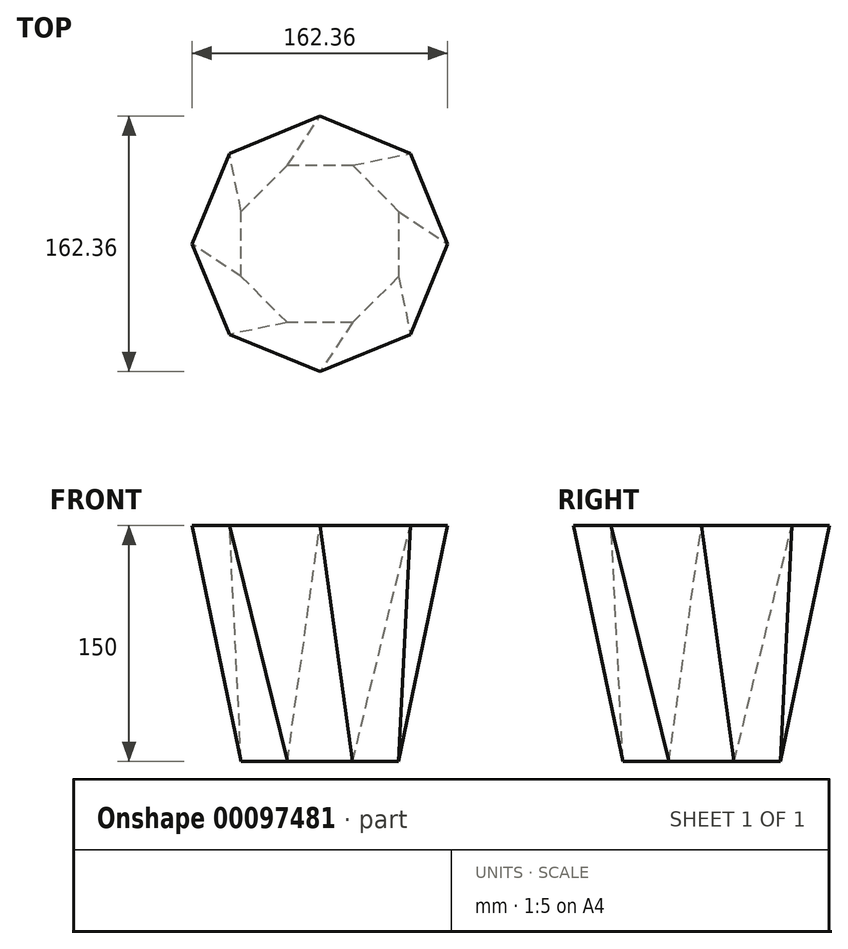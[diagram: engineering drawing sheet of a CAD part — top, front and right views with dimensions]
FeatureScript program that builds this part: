
annotation { "Feature Type Name" : "Feature", "Feature Type Description" : "" }
export const myFeature = defineFeature(function(context is Context, id is Id, definition is map)
    precondition{}
    {
        {
            assignVariable(context, id + "F0", {"name" : "height", "anyValue" : 150});
        }
        {
            var Q0;
            Q0=qCreatedBy(makeId("Top.planeOp"),FACE);
            var sketch = newSketch(context, id + "F1", { "sketchPlane" : qUnion([Q0])});
            skCircle(sketch, "E0.cCircle", {"center": v(0, 0) * mm, "radius": 50 * mm, "construction": true});
            skLineSegment(sketch, "E0.0", {"start": v(-50, 20.71) * mm, "end": v(-20.71, 50) * mm});
            skLineSegment(sketch, "E0.1", {"start": v(-20.71, 50) * mm, "end": v(20.71, 50) * mm});
            skLineSegment(sketch, "E0.2", {"start": v(20.71, 50) * mm, "end": v(50, 20.71) * mm});
            skLineSegment(sketch, "E0.3", {"start": v(50, 20.71) * mm, "end": v(50, -20.71) * mm});
            skLineSegment(sketch, "E0.4", {"start": v(50, -20.71) * mm, "end": v(20.71, -50) * mm});
            skLineSegment(sketch, "E0.5", {"start": v(20.71, -50) * mm, "end": v(-20.71, -50) * mm});
            skLineSegment(sketch, "E0.6", {"start": v(-20.71, -50) * mm, "end": v(-50, -20.71) * mm});
            skLineSegment(sketch, "E0.7", {"start": v(-50, -20.71) * mm, "end": v(-50, 20.71) * mm});
            skPoint(sketch, "E0.0.midPoint", {"position": v(-35.36, 35.36) * mm});
            skSolve(sketch);
        }
        {
            var Q0;
            Q0=qCreatedBy(makeId("Top.planeOp"),FACE);
            cPlane(context, id + "F2", {"entities" : qUnion([Q0]), "cplaneType" : CPlaneType.OFFSET, "offset" : (getVariable(context, 'height')) * mm, "width" : 150 * mm, "height" : 150 * mm});
        }
        {
            var Q0;
            Q0=qCreatedBy(id+"F2.planeOp",FACE);
            var sketch = newSketch(context, id + "F3", { "sketchPlane" : qUnion([Q0])});
            skCircle(sketch, "E1.cCircle", {"center": v(0, 0) * mm, "radius": 75 * mm, "construction": true});
            skLineSegment(sketch, "E1.0", {"start": v(-81.18, 0) * mm, "end": v(-57.4, 57.4) * mm});
            skLineSegment(sketch, "E1.1", {"start": v(-57.4, 57.4) * mm, "end": v(0, 81.18) * mm});
            skLineSegment(sketch, "E1.2", {"start": v(0, 81.18) * mm, "end": v(57.4, 57.4) * mm});
            skLineSegment(sketch, "E1.3", {"start": v(57.4, 57.4) * mm, "end": v(81.18, 0) * mm});
            skLineSegment(sketch, "E1.4", {"start": v(81.18, 0) * mm, "end": v(57.4, -57.4) * mm});
            skLineSegment(sketch, "E1.5", {"start": v(57.4, -57.4) * mm, "end": v(0, -81.18) * mm});
            skLineSegment(sketch, "E1.6", {"start": v(0, -81.18) * mm, "end": v(-57.4, -57.4) * mm});
            skLineSegment(sketch, "E1.7", {"start": v(-57.4, -57.4) * mm, "end": v(-81.18, 0) * mm});
            skPoint(sketch, "E1.0.midPoint", {"position": v(-69.3, 28.7) * mm});
            skSolve(sketch);
        }
        {
            var Q0;
            Q0=makeQuery(id+"F1.imprint","IMPRINT",FACE,{"disambiguationData":[TD([[makeQuery(id+"F1.imprint","IMPRINT",EDGE,{"derivedFrom":sQuery(id+"F1.wireOp",EDGE,"E0.0")}),-1.0]])]});
            var Q1;
            Q1=makeQuery(id+"F3.imprint","IMPRINT",FACE,{"disambiguationData":[TD([[makeQuery(id+"F3.imprint","IMPRINT",EDGE,{"derivedFrom":sQuery(id+"F3.wireOp",EDGE,"E1.0")}),-1.0]])]});
            loft(context, id + "F4", {"sheetProfilesArray" : [{ "sheetProfileEntities" : qUnion([Q0]) }, { "sheetProfileEntities" : qUnion([Q1]) }]});
        }
    });
